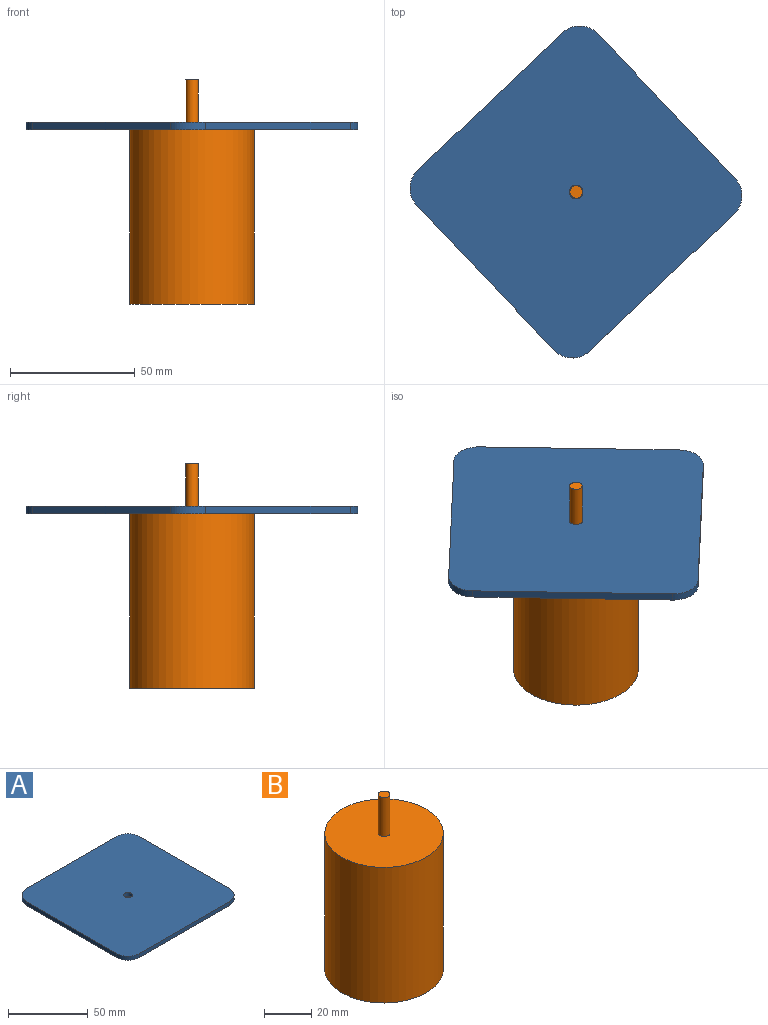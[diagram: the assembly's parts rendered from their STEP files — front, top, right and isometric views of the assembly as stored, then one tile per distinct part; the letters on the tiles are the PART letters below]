
ASSEMBLY  parts=2 mates=1
PART A: 11 faces, bbox 100x100x3 mm
  f0: plane 80x3mm, normal (0,-1,0), area 240mm2, adj f5,f6,f7,f10
  f1: plane 80x3mm, normal (1,0,0), area 240mm2, adj f5,f6,f7,f8
  f2: plane 80x3mm, normal (0,1,0), area 240mm2, adj f5,f6,f8,f9
  f3: cylinder r=2.8mm len=5.6mm, axis (0,0,-1), area 52.8mm2, adj f5,f6
  f4: plane 80x3mm, normal (-1,0,0), area 240mm2, adj f5,f6,f9,f10
  f5: plane 100x100mm, normal (0,0,1), area 9889.5mm2, adj f0,f1,f2,f3,f4,f7,f8,f9
  f6: plane 100x100mm, normal (0,0,-1), area 9889.5mm2, adj f0,f1,f2,f3,f4,f7,f8,f9
  f7: cylinder r=10mm len=10mm, axis (0,0,-1), area 47.1mm2, adj f0,f1,f5,f6
  f8: cylinder r=10mm len=10mm, axis (0,0,1), area 47.1mm2, adj f1,f2,f5,f6
  f9: cylinder r=10mm len=10mm, axis (0,0,-1), area 47.1mm2, adj f2,f4,f5,f6
  f10: cylinder r=10mm len=10mm, axis (0,0,1), area 47.1mm2, adj f0,f4,f5,f6
PART B: 5 faces, bbox 50x50x90 mm
  f0: cylinder r=2.5mm len=20mm, axis (0,0,-1), area 314.2mm2, adj f1,f4
  f1: plane 5x5mm, normal (0,0,1), area 19.6mm2, adj f0
  f2: cylinder r=25mm len=70mm, axis (0,0,1), area 10995.6mm2, adj f3,f4
  f3: plane 50x50mm, normal (0,0,-1), area 1963.5mm2, adj f2
  f4: plane 50x50mm, normal (0,0,1), area 1943.9mm2, adj f0,f2
PLACE A rot(axis=(0,0,1),133.5deg) t=(-22.31,49.12,47.38)mm
PLACE B t=(-22.31,49.12,47.38)mm fixed
MATE revolute B.f0 <-> A.f3  axis (0,0,1) through (-22.31,49.12,47.38)mm
